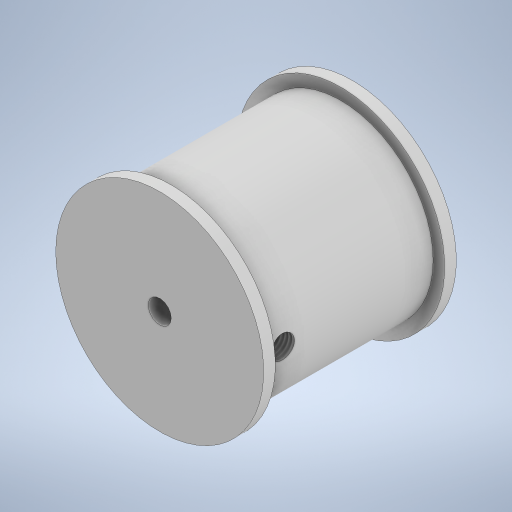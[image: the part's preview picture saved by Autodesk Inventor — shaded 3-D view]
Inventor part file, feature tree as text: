
AUTODESK INVENTOR PART (.ipt)
format: ipt  version: 2024 (Build 280153000, 153)  size: 282,624 bytes
history: native  units: mm
features: sketch x5, extrude x4, other x2, hole x2
ambient origin geometry x8: Origin, YZ Plane, XZ Plane, XY Plane, X Axis, Y Axis, Z Axis, Center Point
bodies: Body1 (feature_tree)
feature tree (13):
  other  "Těleso1"
  sketch  "Náčrt1"
  extrude  "Vysunutí1"  Depth=33.0mm
  hole  "Díra2"  [1 undecoded]
  other  "Závit1"
  extrude  "Vysunutí2"  Depth=25.0mm TaperAngle=0.0deg
  extrude  "Vysunutí3"  Depth=22.0mm TaperAngle=0.0deg
  hole  "Díra1"  [1 undecoded]
  extrude  "Vysunutí4"  Depth=14.5mm TaperAngle=0.0deg
  sketch  "Náčrt2"
  sketch  "Náčrt3"
  sketch  "Náčrt4"
  sketch  "Náčrt5"
note: 2 required parameter values undecoded (feature->parameter linkage not recoverable at this tier; creation-order binding heuristic only, values carry confidence <= 0.55)
